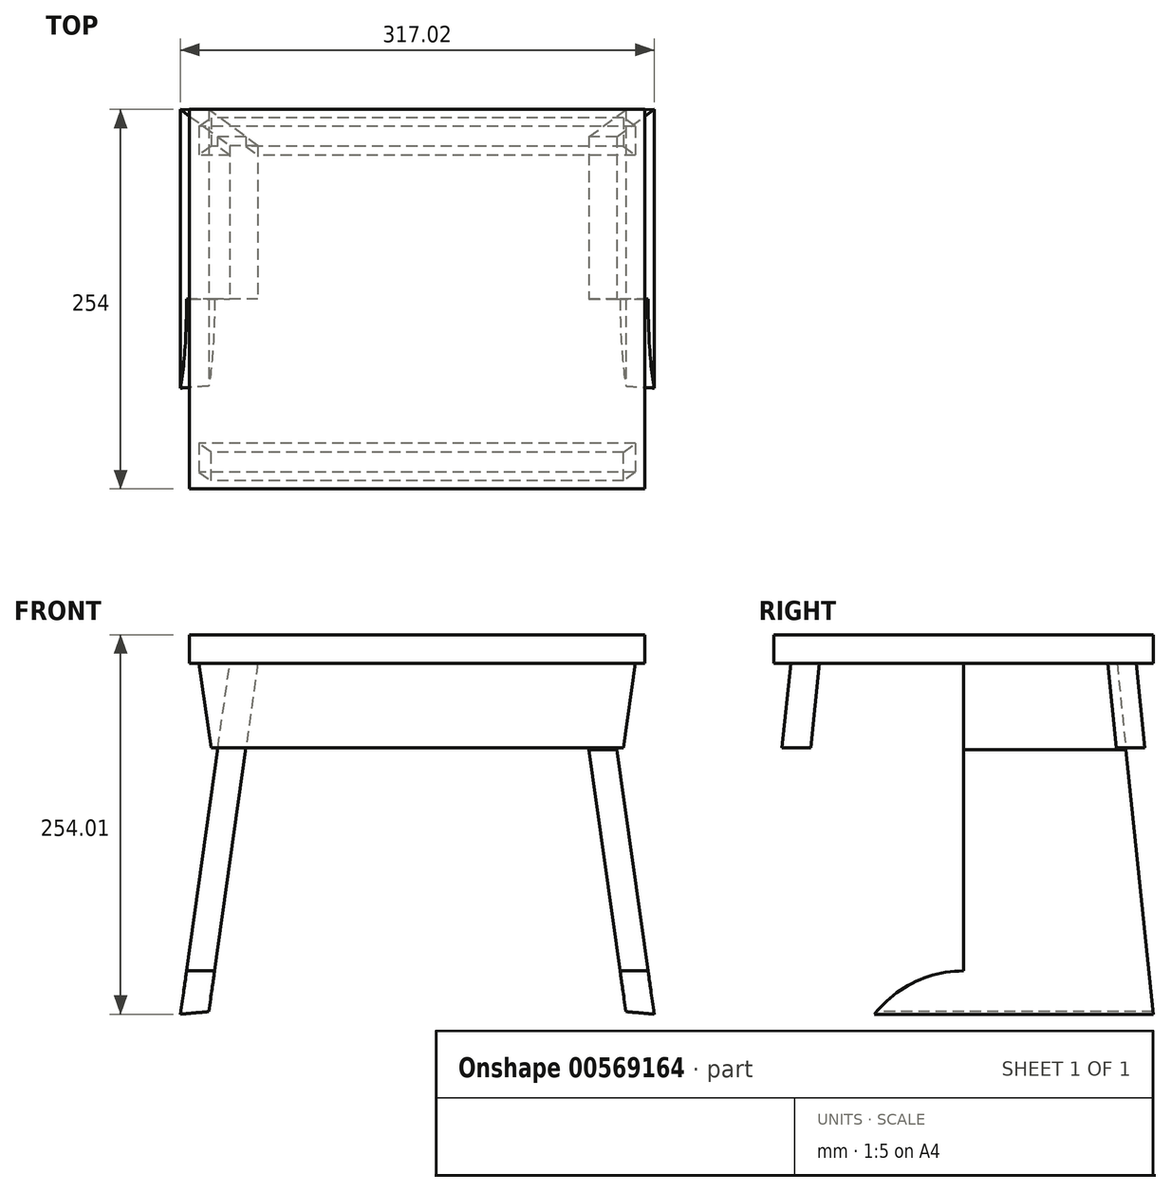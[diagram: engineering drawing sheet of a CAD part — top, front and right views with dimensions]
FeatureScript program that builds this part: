
annotation { "Feature Type Name" : "Feature", "Feature Type Description" : "" }
export const myFeature = defineFeature(function(context is Context, id is Id, definition is map)
    precondition{}
    {
        {
            var Q0;
            Q0=qCreatedBy(makeId("Front.planeOp"),FACE);
            var sketch = newSketch(context, id + "F0", { "sketchPlane" : qUnion([Q0])});
            skLineSegment(sketch, "E0.bottom", {"start": v(152.4, -9.52) * mm, "end": v(-152.4, -9.53) * mm});
            skLineSegment(sketch, "E0.top", {"start": v(152.4, 9.53) * mm, "end": v(-152.4, 9.52) * mm});
            skLineSegment(sketch, "E0.left", {"start": v(152.4, -9.53) * mm, "end": v(152.4, 9.52) * mm});
            skLineSegment(sketch, "E0.right", {"start": v(-152.4, -9.53) * mm, "end": v(-152.4, 9.52) * mm});
            skPoint(sketch, "E0.middle", {"position": v(0, 0) * mm});
            skLineSegment(sketch, "E1.bottom", {"start": v(-152.4, -9.53) * mm, "end": v(152.4, -9.53) * mm, "construction": true});
            skLineSegment(sketch, "E1.top", {"start": v(-152.4, -242.73) * mm, "end": v(152.4, -242.73) * mm, "construction": true});
            skLineSegment(sketch, "E1.left", {"start": v(-152.4, -9.53) * mm, "end": v(-152.4, -242.73) * mm, "construction": true});
            skLineSegment(sketch, "E1.right", {"start": v(152.4, -9.53) * mm, "end": v(152.4, -242.73) * mm, "construction": true});
            skLineSegment(sketch, "E2", {"start": v(158.5, -244.48) * mm, "end": v(139.54, -242.73) * mm});
            skLineSegment(sketch, "E3", {"start": v(0, 0) * mm, "end": v(0, -242.73) * mm, "construction": true});
            skLineSegment(sketch, "E4.MirrorCS", {"start": v(152.4, -9.53) * mm, "end": v(-152.4, -9.53) * mm, "construction": true});
            skLineSegment(sketch, "E5.MirrorCS", {"start": v(-158.5, -244.48) * mm, "end": v(-139.54, -242.73) * mm});
            skLineSegment(sketch, "E6.MirrorCS", {"start": v(-125.49, -9.52) * mm, "end": v(-158.5, -244.48) * mm});
            skLineSegment(sketch, "E7.bottom", {"start": v(-152.4, -9.53) * mm, "end": v(152.4, -9.53) * mm});
            skLineSegment(sketch, "E7.top", {"start": v(-152.4, -67.6) * mm, "end": v(152.4, -67.6) * mm});
            skLineSegment(sketch, "E7.left", {"start": v(-152.4, -9.53) * mm, "end": v(-152.4, -67.6) * mm});
            skLineSegment(sketch, "E7.right", {"start": v(152.4, -9.53) * mm, "end": v(152.4, -67.6) * mm});
            skLineSegment(sketch, "E8", {"start": v(137.89, -67.6) * mm, "end": v(146.05, -9.53) * mm});
            skLineSegment(sketch, "E9.MirrorCS", {"start": v(-137.89, -67.6) * mm, "end": v(-146.05, -9.53) * mm});
            skLineSegment(sketch, "E10", {"start": v(-139.54, -242.73) * mm, "end": v(-106.76, -9.53) * mm});
            skLineSegment(sketch, "E11.MirrorCS", {"start": v(139.54, -242.73) * mm, "end": v(106.76, -9.53) * mm});
            skLineSegment(sketch, "E12.MirrorCS", {"start": v(152.4, -242.73) * mm, "end": v(-152.4, -242.73) * mm, "construction": true});
            skLineSegment(sketch, "E13", {"start": v(158.5, -244.48) * mm, "end": v(125.49, -9.53) * mm});
            skSolve(sketch);
        }
        {
            var Q0;
            Q0=makeQuery(id+"F0.imprint","IMPRINT",FACE,{"disambiguationData":[TD([[makeQuery(id+"F0.imprint","IMPRINT",EDGE,{"derivedFrom":sQuery(id+"F0.wireOp",EDGE,"E0.top")}),1.0]])]});
            extrude(context, id + "F1", {"entities" : qUnion([Q0]), "endBound" : BoundingType.SYMMETRIC, "depth" : 254 * mm, "offsetDistance" : 25.4 * mm});
        }
        {
            var Q0;
            {var subQ0=sQuery(id+"F0.wireOp",EDGE,"E5.MirrorCS");Q0=makeQuery(id+"F0.imprint","IMPRINT",FACE,{"disambiguationData":[TD([[makeQuery(id+"F0.imprint","IMPRINT",EDGE,{"derivedFrom":subQ0}),1.0]])]});}
            var Q1;
            {var subQ0=sQuery(id+"F0.wireOp",EDGE,"E7.bottom");var subQ1=sQuery(id+"F0.wireOp",EDGE,"E6.MirrorCS");var subQ2=makeQuery(id+"F0.imprint","INTERSECT",VERTEX,{"derivedFrom":[subQ1,subQ0]});Q1=makeQuery(id+"F0.imprint","IMPRINT",FACE,{"disambiguationData":[TD([[makeQuery(id+"F0.imprint","IMPRINT",EDGE,{"disambiguationData":[TD([[subQ2,-1.0]])],"derivedFrom":subQ1}),1.0]])]});}
            var Q2;
            {var subQ0=sQuery(id+"F0.wireOp",EDGE,"E11.MirrorCS");var subQ1=sQuery(id+"F0.wireOp",EDGE,"E7.bottom");var subQ2=makeQuery(id+"F0.imprint","INTERSECT",VERTEX,{"derivedFrom":[subQ1,subQ0]});Q2=makeQuery(id+"F0.imprint","IMPRINT",FACE,{"disambiguationData":[TD([[makeQuery(id+"F0.imprint","IMPRINT",EDGE,{"disambiguationData":[TD([[subQ2,-1.0]])],"derivedFrom":subQ1}),-1.0]])]});}
            var Q3;
            {var subQ5=sQuery(id+"F0.wireOp",EDGE,"E2");Q3=makeQuery(id+"F0.imprint","IMPRINT",FACE,{"disambiguationData":[TD([[makeQuery(id+"F0.imprint","IMPRINT",EDGE,{"derivedFrom":subQ5}),-1.0]])]});}
            var Q4;
            Q4=makeQuery(id+"F1.opExtrude","CAP_VERTEX",VERTEX,{"disambiguationData":[OSD([sQuery(id+"F0.wireOp",EDGE,"E0.right"),sQuery(id+"F0.wireOp",EDGE,"E7.bottom"),sQuery(id+"F0.wireOp",EDGE,"E7.left")])],"isStart":true});
            var Q5;
            Q5=makeQuery(id+"F1.opExtrude","CAP_VERTEX",VERTEX,{"disambiguationData":[OSD([sQuery(id+"F0.wireOp",EDGE,"E0.right"),sQuery(id+"F0.wireOp",EDGE,"E7.bottom"),sQuery(id+"F0.wireOp",EDGE,"E7.left")])],"isStart":false});
            extrude(context, id + "F2", {"entities" : qUnion([Q0, Q1, Q2, Q3]), "endBound" : BoundingType.UP_TO_VERTEX, "oppositeDirection" : true, "depth" : 25.4 * mm, "endBoundEntityVertex" : qUnion([Q4]), "offsetDistance" : 25.4 * mm, "hasSecondDirection" : true, "secondDirectionBound" : SecondDirectionBoundingType.UP_TO_VERTEX, "secondDirectionOppositeDirection" : false, "secondDirectionDepth" : 25.4 * mm, "secondDirectionBoundEntityVertex" : qUnion([Q5])});
        }
        {
            var Q0;
            Q0=qCreatedBy(makeId("Right.planeOp"),FACE);
            var sketch = newSketch(context, id + "F3", { "sketchPlane" : qUnion([Q0])});
            skLineSegment(sketch, "E14.0", {"start": v(0, -242.73) * mm, "end": v(0, -9.52) * mm});
            skLineSegment(sketch, "E15.0.0", {"start": v(-127, -244.48) * mm, "end": v(127, -244.48) * mm});
            skLineSegment(sketch, "E15.0.1", {"start": v(127, -244.48) * mm, "end": v(127, -9.52) * mm});
            skLineSegment(sketch, "E15.0.2", {"start": v(127, -9.53) * mm, "end": v(-127, -9.53) * mm});
            skLineSegment(sketch, "E15.0.3", {"start": v(-127, -9.52) * mm, "end": v(-127, -244.48) * mm});
            skLineSegment(sketch, "E16", {"start": v(-127, -244.48) * mm, "end": v(-102.86, -9.52) * mm});
            skLineSegment(sketch, "E17.MirrorCS", {"start": v(127, -9.52) * mm, "end": v(127, -244.48) * mm});
            skLineSegment(sketch, "E18.MirrorCS", {"start": v(127, -244.48) * mm, "end": v(102.86, -9.52) * mm});
            skArc(sketch, "E19", {"start": v(59.47, -244.48) * mm, "mid": v(0, -215.5) * mm, "end": v(-59.47, -244.48) * mm});
            skLineSegment(sketch, "E20", {"start": v(0, -291.04) * mm, "end": v(0, -242.73) * mm, "construction": true});
            skPoint(sketch, "E21", {"position": v(0, -244.48) * mm});
            skSolve(sketch);
        }
        {
            var Q0;
            {var subQ0=sQuery(id+"F3.wireOp",EDGE,"E15.0.3");Q0=makeQuery(id+"F3.imprint","IMPRINT",FACE,{"disambiguationData":[TD([[makeQuery(id+"F3.imprint","IMPRINT",EDGE,{"derivedFrom":subQ0}),1.0]])]});}
            var Q1;
            {var subQ2=sQuery(id+"F3.wireOp",EDGE,"E18.MirrorCS");Q1=makeQuery(id+"F3.imprint","IMPRINT",FACE,{"disambiguationData":[TD([[makeQuery(id+"F3.imprint","IMPRINT",EDGE,{"derivedFrom":subQ2}),-1.0]])]});}
            var Q2;
            {var subQ0=sQuery(id+"F3.wireOp",EDGE,"E19");var subQ1=sQuery(id+"F3.wireOp",EDGE,"E15.0.0");var subQ2=makeQuery(id+"F3.imprint","INTERSECT",VERTEX,{"disambiguationData":[OD(0.0)],"derivedFrom":[subQ1,subQ0]});Q2=makeQuery(id+"F3.imprint","IMPRINT",FACE,{"disambiguationData":[TD([[makeQuery(id+"F3.imprint","IMPRINT",EDGE,{"disambiguationData":[TD([[subQ2,1.0]])],"derivedFrom":subQ1}),1.0]])]});}
            extrude(context, id + "F4", {"entities" : qUnion([Q0, Q1, Q2]), "operationType" : NewBodyOperationType.REMOVE, "endBound" : BoundingType.THROUGH_ALL, "depth" : 25.4 * mm, "offsetDistance" : 25.4 * mm, "hasSecondDirection" : true, "secondDirectionBound" : SecondDirectionBoundingType.THROUGH_ALL, "secondDirectionOppositeDirection" : true, "secondDirectionDepth" : 25.4 * mm});
        }
        {
            var Q0;
            Q0=qCreatedBy(makeId("Right.planeOp"),FACE);
            var sketch = newSketch(context, id + "F5", { "sketchPlane" : qUnion([Q0])});
            skLineSegment(sketch, "E22.0", {"start": v(-102.86, -9.53) * mm, "end": v(-127, -244.48) * mm});
            skLineSegment(sketch, "E23.0", {"start": v(-127, -9.53) * mm, "end": v(127, -9.53) * mm});
            skLineSegment(sketch, "E24.0", {"start": v(102.86, -9.52) * mm, "end": v(127, -244.48) * mm});
            skLineSegment(sketch, "E25", {"start": v(-115.62, -9.53) * mm, "end": v(-121.44, -66.14) * mm});
            skLineSegment(sketch, "E26", {"start": v(-121.44, -66.14) * mm, "end": v(-102.3, -66.14) * mm});
            skLineSegment(sketch, "E27", {"start": v(-102.3, -66.14) * mm, "end": v(-96.47, -9.53) * mm});
            skLineSegment(sketch, "E28", {"start": v(-96.47, -9.52) * mm, "end": v(-115.62, -9.52) * mm});
            skLineSegment(sketch, "E29", {"start": v(-102.3, -66.14) * mm, "end": v(9.56, -67.73) * mm, "construction": true});
            skLineSegment(sketch, "E30.MirrorCS", {"start": v(121.44, -66.14) * mm, "end": v(102.3, -66.14) * mm});
            skLineSegment(sketch, "E31.MirrorCS", {"start": v(96.47, -9.52) * mm, "end": v(115.62, -9.52) * mm});
            skLineSegment(sketch, "E32.MirrorCS", {"start": v(127, -9.52) * mm, "end": v(-127, -9.52) * mm});
            skLineSegment(sketch, "E33.MirrorCS", {"start": v(115.62, -9.53) * mm, "end": v(121.44, -66.14) * mm});
            skLineSegment(sketch, "E34.MirrorCS", {"start": v(102.3, -66.14) * mm, "end": v(96.47, -9.53) * mm});
            skLineSegment(sketch, "E35.MirrorCS", {"start": v(-102.3, -66.14) * mm, "end": v(9.57, -67.52) * mm, "construction": true});
            skSolve(sketch);
        }
        {
            var Q0;
            {var subQ5=sQuery(id+"F5.wireOp",EDGE,"E25");Q0=makeQuery(id+"F5.imprint","IMPRINT",FACE,{"disambiguationData":[TD([[makeQuery(id+"F5.imprint","IMPRINT",EDGE,{"derivedFrom":subQ5}),1.0]])]});}
            var Q1;
            {var subQ5=sQuery(id+"F5.wireOp",EDGE,"E27");Q1=makeQuery(id+"F5.imprint","IMPRINT",FACE,{"disambiguationData":[TD([[makeQuery(id+"F5.imprint","IMPRINT",EDGE,{"derivedFrom":subQ5}),1.0]])]});}
            var Q2;
            {var subQ5=sQuery(id+"F5.wireOp",EDGE,"E34.MirrorCS");Q2=makeQuery(id+"F5.imprint","IMPRINT",FACE,{"disambiguationData":[TD([[makeQuery(id+"F5.imprint","IMPRINT",EDGE,{"derivedFrom":subQ5}),-1.0]])]});}
            var Q3;
            {var subQ5=sQuery(id+"F5.wireOp",EDGE,"E33.MirrorCS");Q3=makeQuery(id+"F5.imprint","IMPRINT",FACE,{"disambiguationData":[TD([[makeQuery(id+"F5.imprint","IMPRINT",EDGE,{"derivedFrom":subQ5}),-1.0]])]});}
            extrude(context, id + "F6", {"entities" : qUnion([Q0, Q1, Q2, Q3]), "depth" : 152.15 * mm, "offsetDistance" : 25.4 * mm, "hasSecondDirection" : true, "secondDirectionOppositeDirection" : true, "secondDirectionDepth" : 152.15 * mm});
        }
        {
            var Q0;
            {var subQ0=sQuery(id+"F0.wireOp",EDGE,"E7.left");Q0=makeQuery(id+"F0.imprint","IMPRINT",FACE,{"disambiguationData":[TD([[makeQuery(id+"F0.imprint","IMPRINT",EDGE,{"derivedFrom":subQ0}),1.0]])]});}
            var Q1;
            {var subQ0=sQuery(id+"F0.wireOp",EDGE,"E7.right");Q1=makeQuery(id+"F0.imprint","IMPRINT",FACE,{"disambiguationData":[TD([[makeQuery(id+"F0.imprint","IMPRINT",EDGE,{"derivedFrom":subQ0}),-1.0]])]});}
            extrude(context, id + "F7", {"entities" : qUnion([Q0, Q1]), "operationType" : NewBodyOperationType.REMOVE, "endBound" : BoundingType.THROUGH_ALL, "oppositeDirection" : true, "depth" : 25.4 * mm, "offsetDistance" : 25.4 * mm, "hasSecondDirection" : true, "secondDirectionBound" : SecondDirectionBoundingType.THROUGH_ALL, "secondDirectionOppositeDirection" : false, "secondDirectionDepth" : 25.4 * mm});
        }
        {
            var Q0;
            Q0=makeQuery(id+"F2.opExtrude","SWEPT_BODY",BODY,{"disambiguationData":[OSD([sQuery(id+"F0.wireOp",EDGE,"E7.bottom"),sQuery(id+"F0.wireOp",EDGE,"E2"),sQuery(id+"F0.wireOp",EDGE,"E11.MirrorCS"),sQuery(id+"F0.wireOp",EDGE,"E13")])]});
            var Q1;
            Q1=makeQuery(id+"F6.opExtrude","SWEPT_BODY",BODY,{"disambiguationData":[OSD([sQuery(id+"F5.wireOp",EDGE,"E25"),sQuery(id+"F5.wireOp",EDGE,"E26"),sQuery(id+"F5.wireOp",EDGE,"E27"),sQuery(id+"F5.wireOp",EDGE,"E32.MirrorCS")])]});
            booleanBodies(context, id + "F8", {"operationType" : BooleanOperationType.SUBTRACTION, "tools" : qUnion([Q0]), "targets" : qUnion([Q1]), "keepTools" : true});
        }
        {
            var Q0;
            Q0=makeQuery(id+"F2.opExtrude","SWEPT_BODY",BODY,{"disambiguationData":[OSD([sQuery(id+"F0.wireOp",EDGE,"E7.bottom"),sQuery(id+"F0.wireOp",EDGE,"E2"),sQuery(id+"F0.wireOp",EDGE,"E11.MirrorCS"),sQuery(id+"F0.wireOp",EDGE,"E13")])]});
            var Q1;
            Q1=makeQuery(id+"F6.opExtrude","SWEPT_BODY",BODY,{"disambiguationData":[OSD([sQuery(id+"F5.wireOp",EDGE,"E33.MirrorCS"),sQuery(id+"F5.wireOp",EDGE,"E30.MirrorCS"),sQuery(id+"F5.wireOp",EDGE,"E34.MirrorCS"),sQuery(id+"F5.wireOp",EDGE,"E31.MirrorCS")])]});
            booleanBodies(context, id + "F9", {"operationType" : BooleanOperationType.SUBTRACTION, "tools" : qUnion([Q0]), "targets" : qUnion([Q1]), "keepTools" : true});
        }
        {
            var Q0;
            Q0=makeQuery(id+"F2.opExtrude","SWEPT_BODY",BODY,{"disambiguationData":[OSD([sQuery(id+"F0.wireOp",EDGE,"E5.MirrorCS"),sQuery(id+"F0.wireOp",EDGE,"E6.MirrorCS"),sQuery(id+"F0.wireOp",EDGE,"E7.bottom"),sQuery(id+"F0.wireOp",EDGE,"E10")])]});
            var Q1;
            Q1=makeQuery(id+"F6.opExtrude","SWEPT_BODY",BODY,{"disambiguationData":[OSD([sQuery(id+"F5.wireOp",EDGE,"E25"),sQuery(id+"F5.wireOp",EDGE,"E26"),sQuery(id+"F5.wireOp",EDGE,"E27"),sQuery(id+"F5.wireOp",EDGE,"E32.MirrorCS")])]});
            booleanBodies(context, id + "F10", {"operationType" : BooleanOperationType.SUBTRACTION, "tools" : qUnion([Q0]), "targets" : qUnion([Q1]), "keepTools" : true});
        }
        {
            var Q0;
            Q0=makeQuery(id+"F2.opExtrude","SWEPT_BODY",BODY,{"disambiguationData":[OSD([sQuery(id+"F0.wireOp",EDGE,"E5.MirrorCS"),sQuery(id+"F0.wireOp",EDGE,"E6.MirrorCS"),sQuery(id+"F0.wireOp",EDGE,"E7.bottom"),sQuery(id+"F0.wireOp",EDGE,"E10")])]});
            var Q1;
            Q1=makeQuery(id+"F6.opExtrude","SWEPT_BODY",BODY,{"disambiguationData":[OSD([sQuery(id+"F5.wireOp",EDGE,"E33.MirrorCS"),sQuery(id+"F5.wireOp",EDGE,"E30.MirrorCS"),sQuery(id+"F5.wireOp",EDGE,"E34.MirrorCS"),sQuery(id+"F5.wireOp",EDGE,"E31.MirrorCS")])]});
            booleanBodies(context, id + "F11", {"operationType" : BooleanOperationType.SUBTRACTION, "tools" : qUnion([Q0]), "targets" : qUnion([Q1]), "keepTools" : true});
        }
    });
